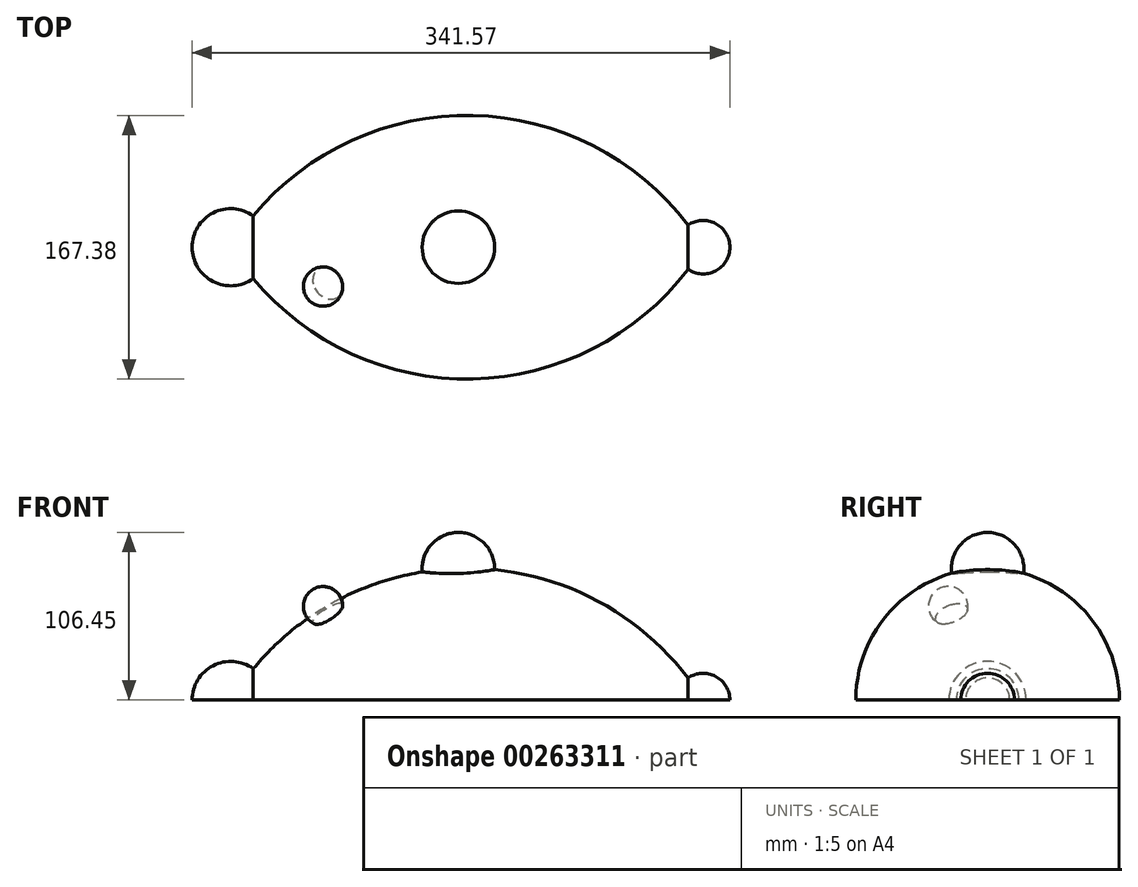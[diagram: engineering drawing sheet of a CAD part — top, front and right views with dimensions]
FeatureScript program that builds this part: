
annotation { "Feature Type Name" : "Feature", "Feature Type Description" : "" }
export const myFeature = defineFeature(function(context is Context, id is Id, definition is map)
    precondition{}
    {
        {
            var Q0;
            Q0=qCreatedBy(makeId("Front.planeOp"),FACE);
            var sketch = newSketch(context, id + "F0", { "sketchPlane" : qUnion([Q0])});
            skLineSegment(sketch, "E0", {"start": v(-125.45, 0) * mm, "end": v(0, 0) * mm});
            skLineSegment(sketch, "E1", {"start": v(0, 0) * mm, "end": v(150, 0) * mm});
            skArc(sketch, "E2", {"start": v(140.37, 14.03) * mm, "mid": v(3.77, 83.65) * mm, "end": v(-135.68, 19.94) * mm});
            skArc(sketch, "E3", {"start": v(-135.68, 19.94) * mm, "mid": v(-161.2, 21.84) * mm, "end": v(-174.55, 0) * mm});
            skArc(sketch, "E4", {"start": v(167.02, 0) * mm, "mid": v(157.93, 15.06) * mm, "end": v(140.37, 14.03) * mm});
            skLineSegment(sketch, "E5", {"start": v(-125.45, 0) * mm, "end": v(-174.55, 0) * mm});
            skLineSegment(sketch, "E6", {"start": v(150, 0) * mm, "end": v(167.02, 0) * mm});
            skSolve(sketch);
        }
        {
            var Q0;
            Q0=makeQuery(id+"F0.imprint","IMPRINT",FACE,{"disambiguationData":[TD([[makeQuery(id+"F0.imprint","IMPRINT",EDGE,{"derivedFrom":sQuery(id+"F0.wireOp",EDGE,"E0")}),1.0]])]});
            var Q1;
            Q1=sQuery(id+"F0.wireOp",EDGE,"E1");
            revolve(context, id + "F1", {"entities" : qUnion([Q0]), "axis" : qUnion([Q1]), "revolveType" : RevolveType.SYMMETRIC, "angle" : 180 * degree});
        }
        {
            var Q0;
            Q0=qCreatedBy(makeId("Front.planeOp"),FACE);
            var sketch = newSketch(context, id + "F2", { "sketchPlane" : qUnion([Q0])});
            skLineSegment(sketch, "E7.0.0", {"start": v(-135.68, 0) * mm, "end": v(-135.68, 19.94) * mm, "construction": true});
            skLineSegment(sketch, "E7.0.1", {"start": v(-135.68, 0) * mm, "end": v(140.37, 0) * mm, "construction": true});
            skLineSegment(sketch, "E7.0.2", {"start": v(140.37, 0) * mm, "end": v(140.37, 14.03) * mm, "construction": true});
            skLineSegment(sketch, "E7.0.3", {"start": v(140.37, 0) * mm, "end": v(-135.68, 0) * mm, "construction": true});
            skLineSegment(sketch, "E8", {"start": v(-5.43, 83.45) * mm, "end": v(-5.43, 106.45) * mm});
            skLineSegment(sketch, "E9", {"start": v(-5.43, 83.45) * mm, "end": v(-5.43, 60.45) * mm});
            skArc(sketch, "E10", {"start": v(-5.43, 60.45) * mm, "mid": v(17.57, 83.45) * mm, "end": v(-5.43, 106.45) * mm});
            skSolve(sketch);
        }
        {
            var Q0;
            Q0=makeQuery(id+"F2.imprint","IMPRINT",FACE,{"disambiguationData":[TD([[makeQuery(id+"F2.imprint","IMPRINT",EDGE,{"derivedFrom":sQuery(id+"F2.wireOp",EDGE,"E8")}),-1.0]])]});
            var Q1;
            Q1=sQuery(id+"F2.wireOp",EDGE,"E8");
            revolve(context, id + "F3", {"operationType" : NewBodyOperationType.ADD, "entities" : qUnion([Q0]), "axis" : qUnion([Q1]), "revolveType" : RevolveType.FULL});
        }
        {
            var Q0;
            Q0=qCreatedBy(makeId("Front.planeOp"),FACE);
            cPlane(context, id + "F4", {"entities" : qUnion([Q0]), "cplaneType" : CPlaneType.OFFSET, "offset" : 25 * mm, "width" : 150 * mm, "height" : 150 * mm});
        }
        {
            var Q0;
            Q0=qCreatedBy(id+"F4.planeOp",FACE);
            var sketch = newSketch(context, id + "F5", { "sketchPlane" : qUnion([Q0])});
            skArc(sketch, "E11", {"start": v(-91.36, 47.1) * mm, "mid": v(-78.86, 59.6) * mm, "end": v(-91.36, 72.1) * mm});
            skLineSegment(sketch, "E12", {"start": v(-91.36, 72.1) * mm, "end": v(-91.36, 47.1) * mm});
            skSolve(sketch);
        }
        {
            var Q0;
            Q0=makeQuery(id+"F5.imprint","IMPRINT",FACE,{"disambiguationData":[TD([[makeQuery(id+"F5.imprint","IMPRINT",EDGE,{"derivedFrom":sQuery(id+"F5.wireOp",EDGE,"E11")}),1.0]])]});
            var Q1;
            Q1=sQuery(id+"F5.wireOp",EDGE,"E12");
            revolve(context, id + "F6", {"operationType" : NewBodyOperationType.ADD, "entities" : qUnion([Q0]), "axis" : qUnion([Q1]), "revolveType" : RevolveType.FULL});
        }
    });
